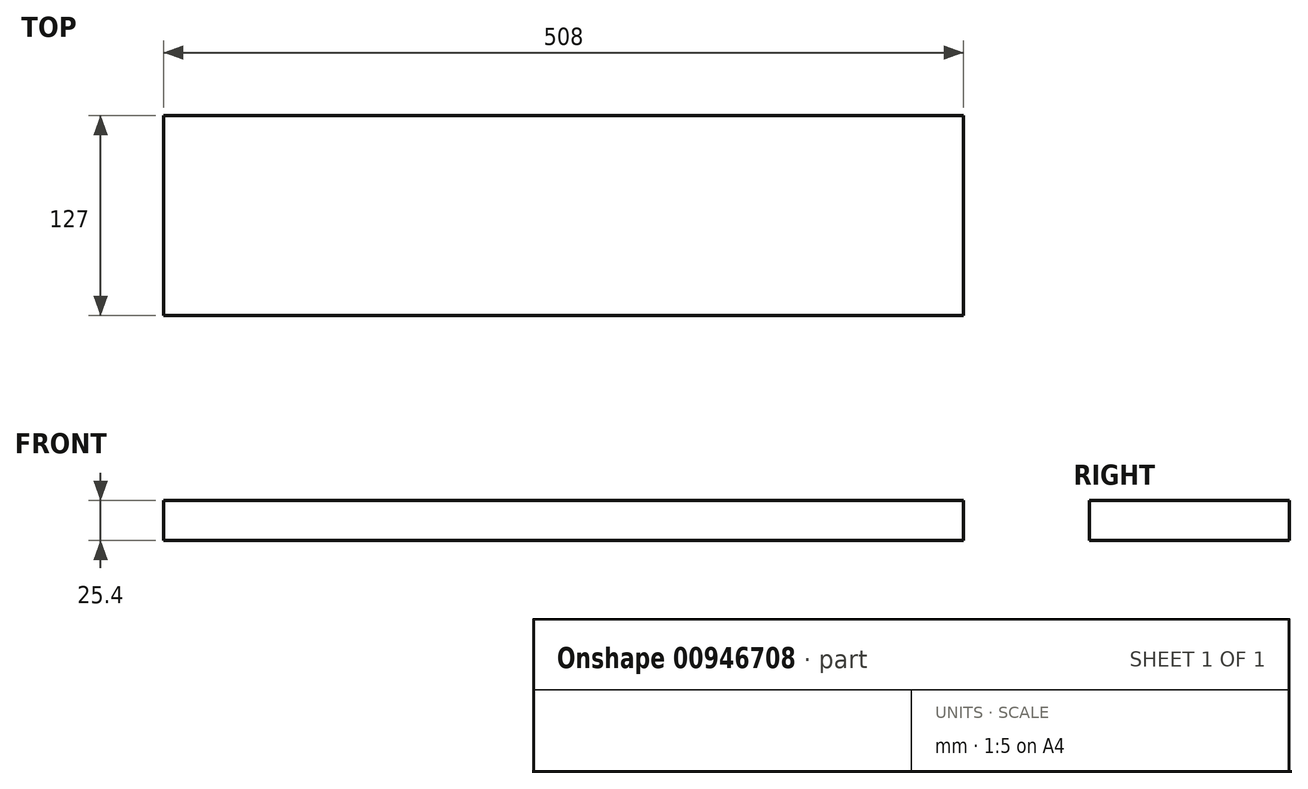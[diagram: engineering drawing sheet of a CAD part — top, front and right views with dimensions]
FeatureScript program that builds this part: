
annotation { "Feature Type Name" : "Feature", "Feature Type Description" : "" }
export const myFeature = defineFeature(function(context is Context, id is Id, definition is map)
    precondition{}
    {
        {
            var Q0;
            Q0=qCreatedBy(makeId("Top.planeOp"),FACE);
            var sketch = newSketch(context, id + "F0", { "sketchPlane" : qUnion([Q0])});
            skLineSegment(sketch, "E0.bottom", {"start": v(254, 63.5) * mm, "end": v(-254, 63.5) * mm});
            skLineSegment(sketch, "E0.top", {"start": v(254, -63.5) * mm, "end": v(-254, -63.5) * mm});
            skLineSegment(sketch, "E0.left", {"start": v(254, 63.5) * mm, "end": v(254, -63.5) * mm});
            skLineSegment(sketch, "E0.right", {"start": v(-254, 63.5) * mm, "end": v(-254, -63.5) * mm});
            skPoint(sketch, "E0.middle", {"position": v(0, 0) * mm});
            skSolve(sketch);
        }
        {
            var Q0;
            Q0=qSketchRegion(id+"F0",true);
            extrude(context, id + "F1", {"entities" : qUnion([Q0]), "depth" : 25.4 * mm, "offsetDistance" : 25.4 * mm});
        }
    });
